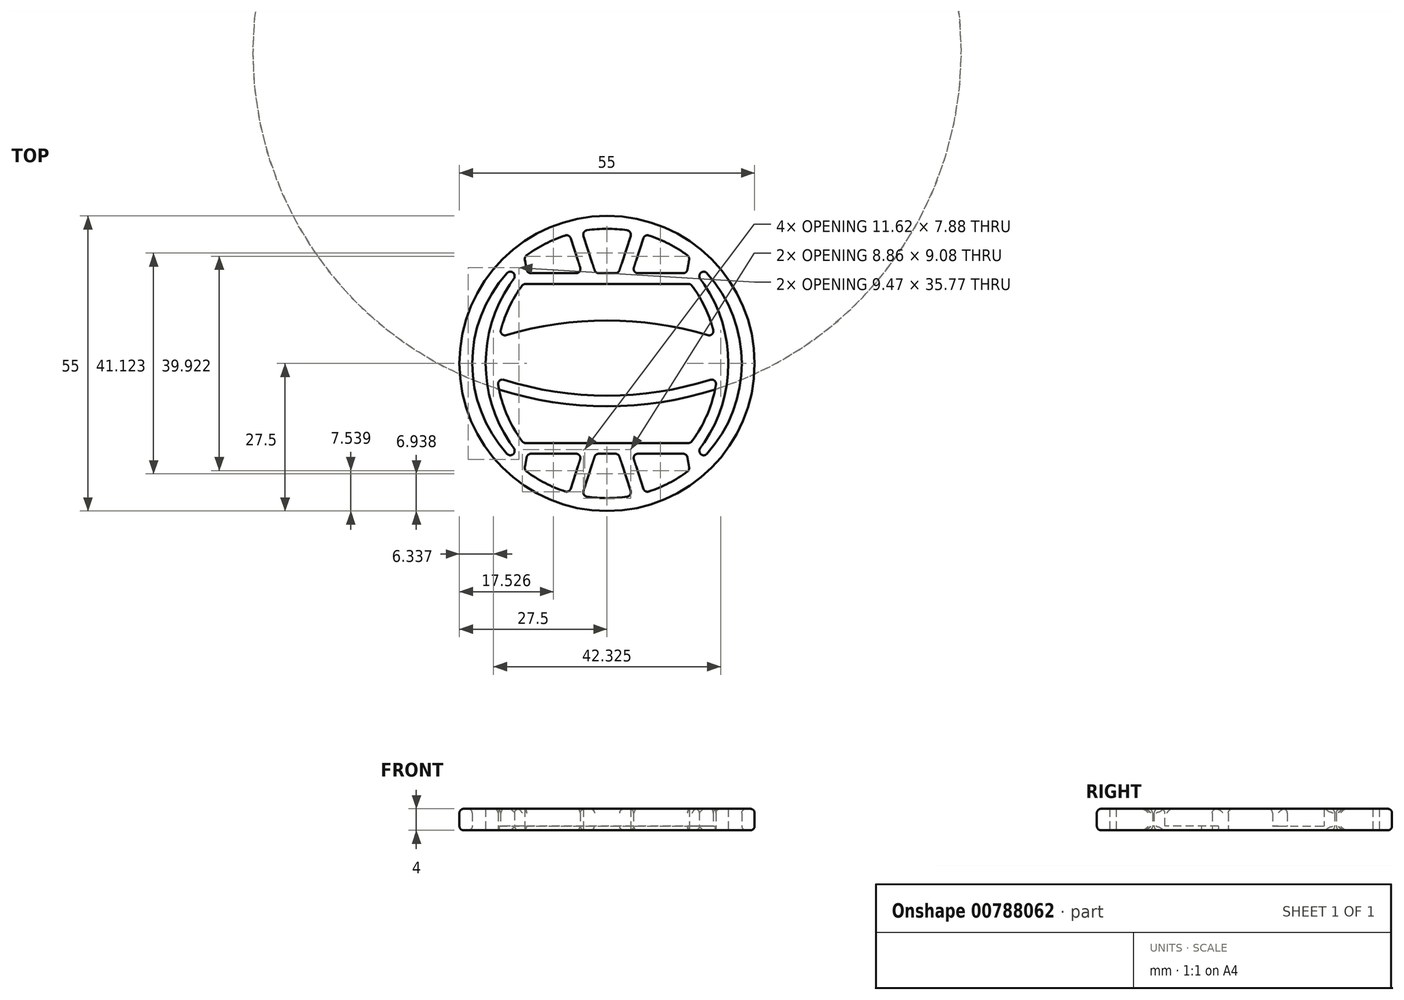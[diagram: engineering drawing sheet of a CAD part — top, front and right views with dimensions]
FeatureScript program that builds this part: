
annotation { "Feature Type Name" : "Feature", "Feature Type Description" : "" }
export const myFeature = defineFeature(function(context is Context, id is Id, definition is map)
    precondition{}
    {
        {
            var Q0;
            Q0=qCreatedBy(makeId("Top.planeOp"),FACE);
            var sketch = newSketch(context, id + "F0", { "sketchPlane" : qUnion([Q0])});
            skCircle(sketch, "E0", {"center": v(0, 0) * mm, "radius": 27.5 * mm});
            skCircle(sketch, "E1.0", {"center": v(0, 0) * mm, "radius": 25.1 * mm});
            skLineSegment(sketch, "E2", {"start": v(0, 12.84) * mm, "end": v(0, -12.84) * mm, "construction": true});
            skLineSegment(sketch, "E3", {"start": v(-3.75, 0) * mm, "end": v(3.75, 0) * mm, "construction": true});
            skArc(sketch, "E4", {"start": v(-17.15, 16.04) * mm, "mid": v(-22.6, 0) * mm, "end": v(-17.15, -16.04) * mm});
            skLineSegment(sketch, "E5", {"start": v(-17.15, 16.04) * mm, "end": v(3.75, 0) * mm, "construction": true});
            skLineSegment(sketch, "E6", {"start": v(3.75, 0) * mm, "end": v(-17.15, -16.04) * mm, "construction": true});
            skArc(sketch, "E7.0", {"start": v(-15.57, 14.82) * mm, "mid": v(-20.6, 0) * mm, "end": v(-15.57, -14.82) * mm});
            skArc(sketch, "E8.MirrorCS", {"start": v(17.15, 16.04) * mm, "mid": v(22.6, 0) * mm, "end": v(17.15, -16.04) * mm});
            skArc(sketch, "E9.MirrorCS", {"start": v(15.57, 14.82) * mm, "mid": v(20.6, 0) * mm, "end": v(15.57, -14.82) * mm});
            skLineSegment(sketch, "E10", {"start": v(-15.57, 14.82) * mm, "end": v(15.57, 14.82) * mm});
            skLineSegment(sketch, "E11", {"start": v(-15.57, -14.82) * mm, "end": v(15.57, -14.82) * mm});
            skArc(sketch, "E12", {"start": v(20.46, 2.64) * mm, "mid": v(0, 6) * mm, "end": v(-20.46, 2.64) * mm});
            skLineSegment(sketch, "E13", {"start": v(-17.5, 18) * mm, "end": v(-17.15, 16.04) * mm});
            skLineSegment(sketch, "E14", {"start": v(-15.39, 19.83) * mm, "end": v(-14.86, 16.82) * mm});
            skLineSegment(sketch, "E15", {"start": v(-14.86, 16.82) * mm, "end": v(0, 16.82) * mm});
            skLineSegment(sketch, "E16", {"start": v(-7.02, 24.1) * mm, "end": v(-4.66, 16.82) * mm});
            skLineSegment(sketch, "E17", {"start": v(-4.68, 24.66) * mm, "end": v(-2.13, 16.82) * mm});
            skLineSegment(sketch, "E18.MirrorCS", {"start": v(14.86, 16.82) * mm, "end": v(0, 16.82) * mm});
            skLineSegment(sketch, "E19.MirrorCS", {"start": v(4.68, 24.66) * mm, "end": v(2.13, 16.82) * mm});
            skLineSegment(sketch, "E20.MirrorCS", {"start": v(7.02, 24.1) * mm, "end": v(4.66, 16.82) * mm});
            skLineSegment(sketch, "E21.MirrorCS", {"start": v(17.5, 18) * mm, "end": v(17.15, 16.04) * mm});
            skLineSegment(sketch, "E22.MirrorCS", {"start": v(15.39, 19.83) * mm, "end": v(14.86, 16.82) * mm});
            skPoint(sketch, "E23", {"position": v(0, 6) * mm});
            skArc(sketch, "E24", {"start": v(-20.1, 4.86) * mm, "mid": v(0, 8) * mm, "end": v(20.1, 4.86) * mm});
            skPoint(sketch, "E25", {"position": v(0, 8) * mm});
            skArc(sketch, "E26.MirrorCS", {"start": v(20.46, -2.64) * mm, "mid": v(0, -6) * mm, "end": v(-20.46, -2.64) * mm});
            skArc(sketch, "E27.MirrorCS", {"start": v(-20.1, -4.86) * mm, "mid": v(0, -8) * mm, "end": v(20.1, -4.86) * mm});
            skLineSegment(sketch, "E28.MirrorCS", {"start": v(17.5, -18) * mm, "end": v(17.15, -16.04) * mm});
            skLineSegment(sketch, "E29.MirrorCS", {"start": v(-17.5, -18) * mm, "end": v(-17.15, -16.04) * mm});
            skLineSegment(sketch, "E30.MirrorCS", {"start": v(-15.39, -19.83) * mm, "end": v(-14.86, -16.82) * mm});
            skLineSegment(sketch, "E31.MirrorCS", {"start": v(14.86, -16.82) * mm, "end": v(0, -16.82) * mm});
            skLineSegment(sketch, "E32.MirrorCS", {"start": v(4.68, -24.66) * mm, "end": v(2.13, -16.82) * mm});
            skLineSegment(sketch, "E33.MirrorCS", {"start": v(7.02, -24.1) * mm, "end": v(4.66, -16.82) * mm});
            skLineSegment(sketch, "E34.MirrorCS", {"start": v(-14.86, -16.82) * mm, "end": v(0, -16.82) * mm});
            skLineSegment(sketch, "E35.MirrorCS", {"start": v(-7.02, -24.1) * mm, "end": v(-4.66, -16.82) * mm});
            skLineSegment(sketch, "E36.MirrorCS", {"start": v(15.39, -19.83) * mm, "end": v(14.86, -16.82) * mm});
            skLineSegment(sketch, "E37.MirrorCS", {"start": v(-4.68, -24.66) * mm, "end": v(-2.13, -16.82) * mm});
            skSolve(sketch);
        }
        {
            var Q0;
            Q0=makeQuery(id+"F0.imprint","IMPRINT",FACE,{"disambiguationData":[TD([[makeQuery(id+"F0.imprint","IMPRINT",EDGE,{"derivedFrom":sQuery(id+"F0.wireOp",EDGE,"E4")}),1.0]])]});
            var Q1;
            Q1=makeQuery(id+"F0.imprint","IMPRINT",FACE,{"disambiguationData":[TD([[makeQuery(id+"F0.imprint","IMPRINT",EDGE,{"derivedFrom":sQuery(id+"F0.wireOp",EDGE,"E0")}),1.0]])]});
            var Q2;
            {var subQ0=sQuery(id+"F0.wireOp",EDGE,"E16");Q2=makeQuery(id+"F0.imprint","IMPRINT",FACE,{"disambiguationData":[TD([[makeQuery(id+"F0.imprint","IMPRINT",EDGE,{"derivedFrom":subQ0}),1.0]])]});}
            var Q3;
            {var subQ0=sQuery(id+"F0.wireOp",EDGE,"E19.MirrorCS");Q3=makeQuery(id+"F0.imprint","IMPRINT",FACE,{"disambiguationData":[TD([[makeQuery(id+"F0.imprint","IMPRINT",EDGE,{"derivedFrom":subQ0}),1.0]])]});}
            var Q4;
            {var subQ0=sQuery(id+"F0.wireOp",EDGE,"E35.MirrorCS");Q4=makeQuery(id+"F0.imprint","IMPRINT",FACE,{"disambiguationData":[TD([[makeQuery(id+"F0.imprint","IMPRINT",EDGE,{"derivedFrom":subQ0}),-1.0]])]});}
            var Q5;
            {var subQ0=sQuery(id+"F0.wireOp",EDGE,"E32.MirrorCS");Q5=makeQuery(id+"F0.imprint","IMPRINT",FACE,{"disambiguationData":[TD([[makeQuery(id+"F0.imprint","IMPRINT",EDGE,{"derivedFrom":subQ0}),-1.0]])]});}
            var Q6;
            {var subQ0=sQuery(id+"F0.wireOp",EDGE,"E12");Q6=makeQuery(id+"F0.imprint","IMPRINT",FACE,{"disambiguationData":[TD([[makeQuery(id+"F0.imprint","IMPRINT",EDGE,{"derivedFrom":subQ0}),-1.0]])]});}
            var Q7;
            {var subQ0=sQuery(id+"F0.wireOp",EDGE,"E26.MirrorCS");Q7=makeQuery(id+"F0.imprint","IMPRINT",FACE,{"disambiguationData":[TD([[makeQuery(id+"F0.imprint","IMPRINT",EDGE,{"derivedFrom":subQ0}),1.0]])]});}
            extrude(context, id + "F1", {"entities" : qUnion([Q0, Q1, Q2, Q3, Q4, Q5, Q6, Q7]), "depth" : 4 * mm, "offsetDistance" : 25 * mm});
        }
        {
            var Q0;
            {var subQ0=sQuery(id+"F0.wireOp",EDGE,"E10");Q0=makeQuery(id+"F0.imprint","IMPRINT",FACE,{"disambiguationData":[TD([[makeQuery(id+"F0.imprint","IMPRINT",EDGE,{"derivedFrom":subQ0}),-1.0]])]});}
            var Q1;
            {var subQ0=sQuery(id+"F0.wireOp",EDGE,"E12");Q1=makeQuery(id+"F0.imprint","IMPRINT",FACE,{"disambiguationData":[TD([[makeQuery(id+"F0.imprint","IMPRINT",EDGE,{"derivedFrom":subQ0}),1.0]])]});}
            var Q2;
            {var subQ0=sQuery(id+"F0.wireOp",EDGE,"E11");Q2=makeQuery(id+"F0.imprint","IMPRINT",FACE,{"disambiguationData":[TD([[makeQuery(id+"F0.imprint","IMPRINT",EDGE,{"derivedFrom":subQ0}),1.0]])]});}
            extrude(context, id + "F2", {"entities" : qUnion([Q0, Q1, Q2]), "operationType" : NewBodyOperationType.ADD, "depth" : 0.8 * mm, "offsetDistance" : 25 * mm});
        }
        {
            var Q0;
            Q0=makeQuery(id+"F1.opExtrude","SWEPT_EDGE",EDGE,{"disambiguationData":[OSD([sQuery(id+"F0.wireOp",EDGE,"E1.0"),sQuery(id+"F0.wireOp",EDGE,"E14")])]});
            var Q1;
            Q1=makeQuery(id+"F1.opExtrude","SWEPT_EDGE",EDGE,{"disambiguationData":[OSD([sQuery(id+"F0.wireOp",EDGE,"E1.0"),sQuery(id+"F0.wireOp",EDGE,"E17")])]});
            var Q2;
            Q2=makeQuery(id+"F1.opExtrude","SWEPT_EDGE",EDGE,{"disambiguationData":[OSD([sQuery(id+"F0.wireOp",EDGE,"E1.0"),sQuery(id+"F0.wireOp",EDGE,"E20.MirrorCS")])]});
            var Q3;
            Q3=makeQuery(id+"F1.opExtrude","SWEPT_EDGE",EDGE,{"disambiguationData":[OSD([sQuery(id+"F0.wireOp",EDGE,"E1.0"),sQuery(id+"F0.wireOp",EDGE,"E21.MirrorCS")])]});
            var Q4;
            Q4=makeQuery(id+"F1.opExtrude","SWEPT_EDGE",EDGE,{"disambiguationData":[OSD([sQuery(id+"F0.wireOp",EDGE,"E8.MirrorCS"),sQuery(id+"F0.wireOp",EDGE,"E21.MirrorCS")])]});
            var Q5;
            Q5=makeQuery(id+"F1.opExtrude","SWEPT_EDGE",EDGE,{"disambiguationData":[OSD([sQuery(id+"F0.wireOp",EDGE,"E8.MirrorCS"),sQuery(id+"F0.wireOp",EDGE,"E28.MirrorCS")])]});
            var Q6;
            Q6=makeQuery(id+"F1.opExtrude","SWEPT_EDGE",EDGE,{"disambiguationData":[OSD([sQuery(id+"F0.wireOp",EDGE,"E1.0"),sQuery(id+"F0.wireOp",EDGE,"E28.MirrorCS")])]});
            var Q7;
            Q7=makeQuery(id+"F1.opExtrude","SWEPT_EDGE",EDGE,{"disambiguationData":[OSD([sQuery(id+"F0.wireOp",EDGE,"E1.0"),sQuery(id+"F0.wireOp",EDGE,"E22.MirrorCS")])]});
            var Q8;
            Q8=makeQuery(id+"F1.opExtrude","SWEPT_EDGE",EDGE,{"disambiguationData":[OSD([sQuery(id+"F0.wireOp",EDGE,"E18.MirrorCS"),sQuery(id+"F0.wireOp",EDGE,"E22.MirrorCS")])]});
            var Q9;
            Q9=makeQuery(id+"F1.opExtrude","SWEPT_EDGE",EDGE,{"disambiguationData":[OSD([sQuery(id+"F0.wireOp",EDGE,"E18.MirrorCS"),sQuery(id+"F0.wireOp",EDGE,"E20.MirrorCS")])]});
            var Q10;
            Q10=makeQuery(id+"F1.opExtrude","SWEPT_EDGE",EDGE,{"disambiguationData":[OSD([sQuery(id+"F0.wireOp",EDGE,"E1.0"),sQuery(id+"F0.wireOp",EDGE,"E19.MirrorCS")])]});
            var Q11;
            Q11=makeQuery(id+"F1.opExtrude","SWEPT_EDGE",EDGE,{"disambiguationData":[OSD([sQuery(id+"F0.wireOp",EDGE,"E18.MirrorCS"),sQuery(id+"F0.wireOp",EDGE,"E19.MirrorCS")])]});
            var Q12;
            Q12=makeQuery(id+"F1.opExtrude","SWEPT_EDGE",EDGE,{"disambiguationData":[OSD([sQuery(id+"F0.wireOp",EDGE,"E15"),sQuery(id+"F0.wireOp",EDGE,"E17")])]});
            var Q13;
            Q13=makeQuery(id+"F1.opExtrude","SWEPT_EDGE",EDGE,{"disambiguationData":[OSD([sQuery(id+"F0.wireOp",EDGE,"E14"),sQuery(id+"F0.wireOp",EDGE,"E15")])]});
            var Q14;
            Q14=makeQuery(id+"F1.opExtrude","SWEPT_EDGE",EDGE,{"disambiguationData":[OSD([sQuery(id+"F0.wireOp",EDGE,"E15"),sQuery(id+"F0.wireOp",EDGE,"E16")])]});
            var Q15;
            Q15=makeQuery(id+"F1.opExtrude","SWEPT_EDGE",EDGE,{"disambiguationData":[OSD([sQuery(id+"F0.wireOp",EDGE,"E1.0"),sQuery(id+"F0.wireOp",EDGE,"E16")])]});
            var Q16;
            Q16=makeQuery(id+"F1.opExtrude","SWEPT_EDGE",EDGE,{"disambiguationData":[OSD([sQuery(id+"F0.wireOp",EDGE,"E1.0"),sQuery(id+"F0.wireOp",EDGE,"E13")])]});
            var Q17;
            Q17=makeQuery(id+"F1.opExtrude","SWEPT_EDGE",EDGE,{"disambiguationData":[OSD([sQuery(id+"F0.wireOp",EDGE,"E4"),sQuery(id+"F0.wireOp",EDGE,"E13")])]});
            var Q18;
            Q18=makeQuery(id+"F1.opExtrude","SWEPT_EDGE",EDGE,{"disambiguationData":[OSD([sQuery(id+"F0.wireOp",EDGE,"E1.0"),sQuery(id+"F0.wireOp",EDGE,"E29.MirrorCS")])]});
            var Q19;
            Q19=makeQuery(id+"F1.opExtrude","SWEPT_EDGE",EDGE,{"disambiguationData":[OSD([sQuery(id+"F0.wireOp",EDGE,"E4"),sQuery(id+"F0.wireOp",EDGE,"E29.MirrorCS")])]});
            var Q20;
            Q20=makeQuery(id+"F1.opExtrude","SWEPT_EDGE",EDGE,{"disambiguationData":[OSD([sQuery(id+"F0.wireOp",EDGE,"E7.0"),sQuery(id+"F0.wireOp",EDGE,"E10")])]});
            var Q21;
            Q21=makeQuery(id+"F1.opExtrude","SWEPT_EDGE",EDGE,{"disambiguationData":[OSD([sQuery(id+"F0.wireOp",EDGE,"E9.MirrorCS"),sQuery(id+"F0.wireOp",EDGE,"E10")])]});
            var Q22;
            Q22=makeQuery(id+"F1.opExtrude","SWEPT_EDGE",EDGE,{"disambiguationData":[OSD([sQuery(id+"F0.wireOp",EDGE,"E9.MirrorCS"),sQuery(id+"F0.wireOp",EDGE,"E24")])]});
            var Q23;
            Q23=makeQuery(id+"F1.opExtrude","SWEPT_EDGE",EDGE,{"disambiguationData":[OSD([sQuery(id+"F0.wireOp",EDGE,"E7.0"),sQuery(id+"F0.wireOp",EDGE,"E24")])]});
            var Q24;
            Q24=makeQuery(id+"F1.opExtrude","SWEPT_EDGE",EDGE,{"disambiguationData":[OSD([sQuery(id+"F0.wireOp",EDGE,"E7.0"),sQuery(id+"F0.wireOp",EDGE,"E26.MirrorCS")])]});
            var Q25;
            Q25=makeQuery(id+"F1.opExtrude","SWEPT_EDGE",EDGE,{"disambiguationData":[OSD([sQuery(id+"F0.wireOp",EDGE,"E9.MirrorCS"),sQuery(id+"F0.wireOp",EDGE,"E26.MirrorCS")])]});
            var Q26;
            Q26=makeQuery(id+"F1.opExtrude","SWEPT_EDGE",EDGE,{"disambiguationData":[OSD([sQuery(id+"F0.wireOp",EDGE,"E9.MirrorCS"),sQuery(id+"F0.wireOp",EDGE,"E12")])]});
            var Q27;
            Q27=makeQuery(id+"F1.opExtrude","SWEPT_EDGE",EDGE,{"disambiguationData":[OSD([sQuery(id+"F0.wireOp",EDGE,"E9.MirrorCS"),sQuery(id+"F0.wireOp",EDGE,"E27.MirrorCS")])]});
            var Q28;
            Q28=makeQuery(id+"F1.opExtrude","SWEPT_EDGE",EDGE,{"disambiguationData":[OSD([sQuery(id+"F0.wireOp",EDGE,"E7.0"),sQuery(id+"F0.wireOp",EDGE,"E27.MirrorCS")])]});
            var Q29;
            Q29=makeQuery(id+"F1.opExtrude","SWEPT_EDGE",EDGE,{"disambiguationData":[OSD([sQuery(id+"F0.wireOp",EDGE,"E7.0"),sQuery(id+"F0.wireOp",EDGE,"E11")])]});
            var Q30;
            Q30=makeQuery(id+"F1.opExtrude","SWEPT_EDGE",EDGE,{"disambiguationData":[OSD([sQuery(id+"F0.wireOp",EDGE,"E9.MirrorCS"),sQuery(id+"F0.wireOp",EDGE,"E11")])]});
            var Q31;
            Q31=makeQuery(id+"F1.opExtrude","SWEPT_EDGE",EDGE,{"disambiguationData":[OSD([sQuery(id+"F0.wireOp",EDGE,"E1.0"),sQuery(id+"F0.wireOp",EDGE,"E36.MirrorCS")])]});
            var Q32;
            Q32=makeQuery(id+"F1.opExtrude","SWEPT_EDGE",EDGE,{"disambiguationData":[OSD([sQuery(id+"F0.wireOp",EDGE,"E31.MirrorCS"),sQuery(id+"F0.wireOp",EDGE,"E36.MirrorCS")])]});
            var Q33;
            Q33=makeQuery(id+"F1.opExtrude","SWEPT_EDGE",EDGE,{"disambiguationData":[OSD([sQuery(id+"F0.wireOp",EDGE,"E1.0"),sQuery(id+"F0.wireOp",EDGE,"E33.MirrorCS")])]});
            var Q34;
            Q34=makeQuery(id+"F1.opExtrude","SWEPT_EDGE",EDGE,{"disambiguationData":[OSD([sQuery(id+"F0.wireOp",EDGE,"E31.MirrorCS"),sQuery(id+"F0.wireOp",EDGE,"E33.MirrorCS")])]});
            var Q35;
            Q35=makeQuery(id+"F1.opExtrude","SWEPT_EDGE",EDGE,{"disambiguationData":[OSD([sQuery(id+"F0.wireOp",EDGE,"E1.0"),sQuery(id+"F0.wireOp",EDGE,"E32.MirrorCS")])]});
            var Q36;
            Q36=makeQuery(id+"F1.opExtrude","SWEPT_EDGE",EDGE,{"disambiguationData":[OSD([sQuery(id+"F0.wireOp",EDGE,"E1.0"),sQuery(id+"F0.wireOp",EDGE,"E37.MirrorCS")])]});
            var Q37;
            Q37=makeQuery(id+"F1.opExtrude","SWEPT_EDGE",EDGE,{"disambiguationData":[OSD([sQuery(id+"F0.wireOp",EDGE,"E31.MirrorCS"),sQuery(id+"F0.wireOp",EDGE,"E32.MirrorCS")])]});
            var Q38;
            Q38=makeQuery(id+"F1.opExtrude","SWEPT_EDGE",EDGE,{"disambiguationData":[OSD([sQuery(id+"F0.wireOp",EDGE,"E34.MirrorCS"),sQuery(id+"F0.wireOp",EDGE,"E37.MirrorCS")])]});
            var Q39;
            Q39=makeQuery(id+"F1.opExtrude","SWEPT_EDGE",EDGE,{"disambiguationData":[OSD([sQuery(id+"F0.wireOp",EDGE,"E7.0"),sQuery(id+"F0.wireOp",EDGE,"E12")])]});
            var Q40;
            Q40=makeQuery(id+"F1.opExtrude","SWEPT_EDGE",EDGE,{"disambiguationData":[OSD([sQuery(id+"F0.wireOp",EDGE,"E34.MirrorCS"),sQuery(id+"F0.wireOp",EDGE,"E35.MirrorCS")])]});
            var Q41;
            Q41=makeQuery(id+"F1.opExtrude","SWEPT_EDGE",EDGE,{"disambiguationData":[OSD([sQuery(id+"F0.wireOp",EDGE,"E1.0"),sQuery(id+"F0.wireOp",EDGE,"E30.MirrorCS")])]});
            var Q42;
            Q42=makeQuery(id+"F1.opExtrude","SWEPT_EDGE",EDGE,{"disambiguationData":[OSD([sQuery(id+"F0.wireOp",EDGE,"E30.MirrorCS"),sQuery(id+"F0.wireOp",EDGE,"E34.MirrorCS")])]});
            var Q43;
            Q43=makeQuery(id+"F1.opExtrude","SWEPT_EDGE",EDGE,{"disambiguationData":[OSD([sQuery(id+"F0.wireOp",EDGE,"E1.0"),sQuery(id+"F0.wireOp",EDGE,"E35.MirrorCS")])]});
            var Q44;
            Q44=makeQuery(id+"F1.opExtrude","CAP_EDGE",EDGE,{"disambiguationData":[OSD([sQuery(id+"F0.wireOp",EDGE,"E0")])],"isStart":true});
            var Q45;
            {var subQ0=sQuery(id+"F0.wireOp",EDGE,"E1.0");Q45=makeQuery(id+"F1.opExtrude","CAP_EDGE",EDGE,{"disambiguationData":[OSD([subQ0]),TDD([makeQuery(id+"F0.imprint","IMPRINT",EDGE,{"disambiguationData":[TD([[makeQuery(id+"F0.imprint","INTERSECT",VERTEX,{"derivedFrom":[subQ0,sQuery(id+"F0.wireOp",EDGE,"E21.MirrorCS")]}),1.0]])],"derivedFrom":subQ0})])],"isStart":true});}
            var Q46;
            {var subQ0=sQuery(id+"F0.wireOp",EDGE,"E1.0");Q46=makeQuery(id+"F1.opExtrude","CAP_EDGE",EDGE,{"disambiguationData":[OSD([subQ0]),TDD([makeQuery(id+"F0.imprint","IMPRINT",EDGE,{"disambiguationData":[TD([[makeQuery(id+"F0.imprint","INTERSECT",VERTEX,{"derivedFrom":[subQ0,sQuery(id+"F0.wireOp",EDGE,"E13")]}),-1.0]])],"derivedFrom":subQ0})])],"isStart":true});}
            var Q47;
            Q47=makeQuery(id+"F1.opExtrude","CAP_EDGE",EDGE,{"disambiguationData":[OSD([sQuery(id+"F0.wireOp",EDGE,"E34.MirrorCS")])],"isStart":true});
            var Q48;
            Q48=makeQuery(id+"F1.opExtrude","CAP_EDGE",EDGE,{"disambiguationData":[OSD([sQuery(id+"F0.wireOp",EDGE,"E31.MirrorCS"),sQuery(id+"F0.wireOp",EDGE,"E34.MirrorCS")])],"isStart":true});
            var Q49;
            Q49=makeQuery(id+"F1.opExtrude","CAP_EDGE",EDGE,{"disambiguationData":[OSD([sQuery(id+"F0.wireOp",EDGE,"E31.MirrorCS")])],"isStart":true});
            var Q50;
            Q50=makeQuery(id+"F1.opExtrude","CAP_EDGE",EDGE,{"disambiguationData":[OSD([sQuery(id+"F0.wireOp",EDGE,"E15")])],"isStart":true});
            var Q51;
            Q51=makeQuery(id+"F1.opExtrude","CAP_EDGE",EDGE,{"disambiguationData":[OSD([sQuery(id+"F0.wireOp",EDGE,"E15"),sQuery(id+"F0.wireOp",EDGE,"E18.MirrorCS")])],"isStart":true});
            var Q52;
            Q52=makeQuery(id+"F1.opExtrude","CAP_EDGE",EDGE,{"disambiguationData":[OSD([sQuery(id+"F0.wireOp",EDGE,"E18.MirrorCS")])],"isStart":true});
            var Q53;
            Q53=makeQuery(id+"F1.opExtrude","CAP_EDGE",EDGE,{"disambiguationData":[OSD([sQuery(id+"F0.wireOp",EDGE,"E0")])],"isStart":false});
            var Q54;
            Q54=makeQuery(id+"F1.opExtrude","CAP_EDGE",EDGE,{"disambiguationData":[OSD([sQuery(id+"F0.wireOp",EDGE,"E15")])],"isStart":false});
            var Q55;
            Q55=makeQuery(id+"F1.opExtrude","CAP_EDGE",EDGE,{"disambiguationData":[OSD([sQuery(id+"F0.wireOp",EDGE,"E15"),sQuery(id+"F0.wireOp",EDGE,"E18.MirrorCS")])],"isStart":false});
            var Q56;
            Q56=makeQuery(id+"F1.opExtrude","CAP_EDGE",EDGE,{"disambiguationData":[OSD([sQuery(id+"F0.wireOp",EDGE,"E18.MirrorCS")])],"isStart":false});
            var Q57;
            Q57=makeQuery(id+"F1.opExtrude","CAP_EDGE",EDGE,{"disambiguationData":[OSD([sQuery(id+"F0.wireOp",EDGE,"E24")])],"isStart":false});
            var Q58;
            Q58=makeQuery(id+"F1.opExtrude","CAP_EDGE",EDGE,{"disambiguationData":[OSD([sQuery(id+"F0.wireOp",EDGE,"E26.MirrorCS")])],"isStart":false});
            var Q59;
            Q59=makeQuery(id+"F1.opExtrude","CAP_EDGE",EDGE,{"disambiguationData":[OSD([sQuery(id+"F0.wireOp",EDGE,"E11")])],"isStart":false});
            var Q60;
            {var subQ0=sQuery(id+"F0.wireOp",EDGE,"E1.0");Q60=makeQuery(id+"F1.opExtrude","CAP_EDGE",EDGE,{"disambiguationData":[OSD([subQ0]),TDD([makeQuery(id+"F0.imprint","IMPRINT",EDGE,{"disambiguationData":[TD([[makeQuery(id+"F0.imprint","INTERSECT",VERTEX,{"derivedFrom":[subQ0,sQuery(id+"F0.wireOp",EDGE,"E13")]}),-1.0]])],"derivedFrom":subQ0})])],"isStart":false});}
            var Q61;
            {var subQ0=sQuery(id+"F0.wireOp",EDGE,"E1.0");Q61=makeQuery(id+"F1.opExtrude","CAP_EDGE",EDGE,{"disambiguationData":[OSD([subQ0]),TDD([makeQuery(id+"F0.imprint","IMPRINT",EDGE,{"disambiguationData":[TD([[makeQuery(id+"F0.imprint","INTERSECT",VERTEX,{"derivedFrom":[subQ0,sQuery(id+"F0.wireOp",EDGE,"E21.MirrorCS")]}),1.0]])],"derivedFrom":subQ0})])],"isStart":false});}
            var Q62;
            Q62=makeQuery(id+"F1.opExtrude","CAP_EDGE",EDGE,{"disambiguationData":[OSD([sQuery(id+"F0.wireOp",EDGE,"E31.MirrorCS")])],"isStart":false});
            var Q63;
            Q63=makeQuery(id+"F1.opExtrude","CAP_EDGE",EDGE,{"disambiguationData":[OSD([sQuery(id+"F0.wireOp",EDGE,"E31.MirrorCS"),sQuery(id+"F0.wireOp",EDGE,"E34.MirrorCS")])],"isStart":false});
            var Q64;
            Q64=makeQuery(id+"F1.opExtrude","CAP_EDGE",EDGE,{"disambiguationData":[OSD([sQuery(id+"F0.wireOp",EDGE,"E34.MirrorCS")])],"isStart":false});
            fillet(context, id + "F3", {"entities" : qUnion([Q0, Q1, Q2, Q3, Q4, Q5, Q6, Q7, Q8, Q9, Q10, Q11, Q12, Q13, Q14, Q15, Q16, Q17, Q18, Q19, Q20, Q21, Q22, Q23, Q24, Q25, Q26, Q27, Q28, Q29, Q30, Q31, Q32, Q33, Q34, Q35, Q36, Q37, Q38, Q39, Q40, Q41, Q42, Q43, Q44, Q45, Q46, Q47, Q48, Q49, Q50, Q51, Q52, Q53, Q54, Q55, Q56, Q57, Q58, Q59, Q60, Q61, Q62, Q63, Q64]), "radius" : 0.8 * mm, "tangentPropagation" : true, "allowEdgeOverflow" : false});
        }
    });
